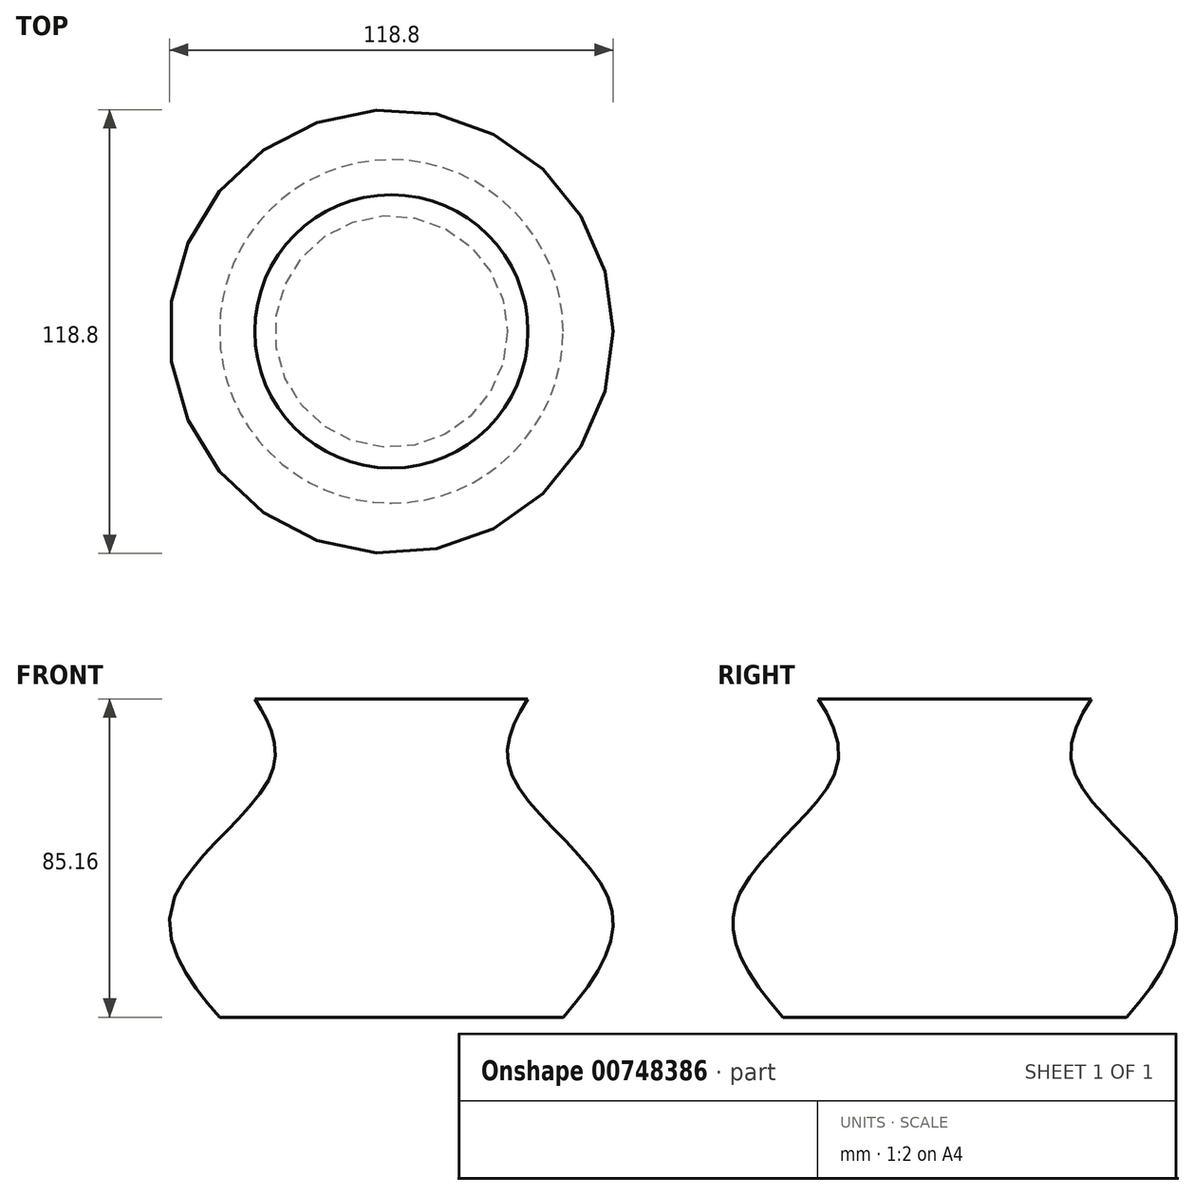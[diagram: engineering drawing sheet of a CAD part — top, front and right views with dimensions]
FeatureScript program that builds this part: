
annotation { "Feature Type Name" : "Feature", "Feature Type Description" : "" }
export const myFeature = defineFeature(function(context is Context, id is Id, definition is map)
    precondition{}
    {
        {
            var Q0;
            Q0=qCreatedBy(makeId("Front.planeOp"),FACE);
            var sketch = newSketch(context, id + "F0", { "sketchPlane" : qUnion([Q0])});
            skFitSpline(sketch, "E0", {"points": [v(42.02, 52.42) * mm, v(31.9, 25.44) * mm, v(58.89, -10.82) * mm, v(33.3, -53.54) * mm], "startDerivative": vector(-71.49, -95.3) * mm, "endDerivative": vector(-118.2, -118.87) * mm});
            skLineSegment(sketch, "E1", {"start": v(-9.13, 44.83) * mm, "end": v(55.51, 44.83) * mm});
            skLineSegment(sketch, "E2", {"start": v(-9.7, -40.33) * mm, "end": v(60, -40.33) * mm});
            skLineSegment(sketch, "E3", {"start": v(0, 58.6) * mm, "end": v(0, -53.54) * mm});
            skSolve(sketch);
        }
        {
            var Q0;
            {var subQ0=sQuery(id+"F0.wireOp",EDGE,"E1");var subQ1=sQuery(id+"F0.wireOp",EDGE,"E0");var subQ2=makeQuery(id+"F0.imprint","INTERSECT",VERTEX,{"derivedFrom":[subQ1,subQ0]});Q0=makeQuery(id+"F0.imprint","IMPRINT",FACE,{"disambiguationData":[TD([[makeQuery(id+"F0.imprint","IMPRINT",EDGE,{"disambiguationData":[TD([[subQ2,-1.0]])],"derivedFrom":subQ1}),-1.0]])]});}
            var Q1;
            Q1=sQuery(id+"F0.wireOp",EDGE,"E3");
            revolve(context, id + "F1", {"surfaceOperationType" : NewSurfaceOperationType.NEW, "entities" : qUnion([Q0]), "axis" : qUnion([Q1]), "revolveType" : RevolveType.FULL});
        }
    });
